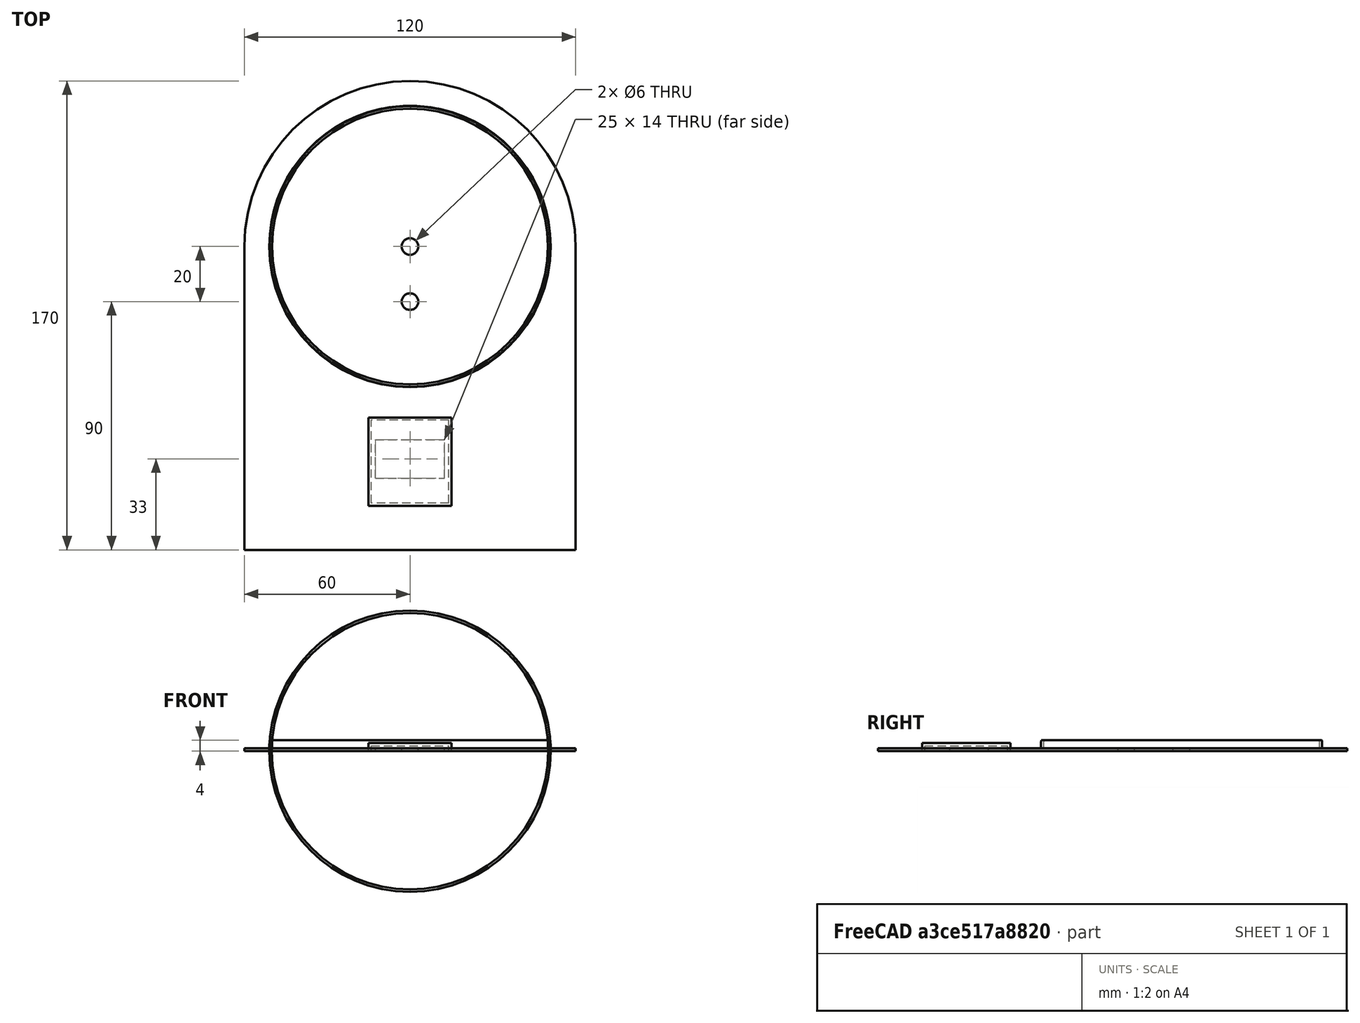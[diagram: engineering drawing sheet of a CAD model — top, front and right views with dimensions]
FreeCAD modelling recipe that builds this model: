
FCSTD DOCUMENT  (FreeCAD 0.16R6703 (Git))
Label: moon_support_v2
License: CreativeCommons Attribution-ShareAlike
LicenseURL: http://creativecommons.org/licenses/by-sa/4.0/
objects: Part::Box×5, Part::Cut×5, Part::Cylinder×3, Part::Sphere×2, Part::MultiFuse×2
note: 17 computed .brp shape members not serialized (recipe doc carries the construction recipe); baked Part::Feature solids carry a one-line shape summary decoded from their .brp

FEATURE [Part::Sphere] Sphere  label="moon"
  Angle1 = -90
  Angle2 = 90
  Angle3 = 180
  Placement = pos=(0,0,0) rot=(1,0,0;1.5708rad)
  Radius = 50.1
FEATURE [Part::Sphere] Sphere001  label="moon_cover"
  Angle1 = -90
  Angle2 = 90
  Angle3 = 180
  Placement = pos=(0,0,0) rot=(1,0,0;1.5708rad)
  Radius = 51
FEATURE [Part::Box] Box  label="recote_soporte"
  Height = 120
  Length = 120
  Placement = pos=(-60,-60,4) rot=(0,0,1;0rad)
  Width = 120
FEATURE [Part::Cut] Cut
  Base = -> Sphere001
  Tool = -> Sphere
FEATURE [Part::Cut] Cut001
  Base = -> Cut
  Tool = -> Box
FEATURE [Part::Cylinder] Cylinder
  Angle = 360
  Height = 20
  Placement = pos=(0,-20,-2) rot=(0,0,1;0rad)
  Radius = 3
FEATURE [Part::Box] Box001  label="Cube"
  Height = 1
  Length = 120
  Placement = pos=(-60,-110,0) rot=(0,0,1;0rad)
  Width = 110
FEATURE [Part::Cylinder] Cylinder001
  Angle = 360
  Height = 1
  Radius = 60
FEATURE [Part::Box] Box002  label="lcd"
  Height = 10
  Length = 25
  Placement = pos=(-12.5,-84,0) rot=(0,0,1;0rad)
  Width = 14
FEATURE [Part::Box] Box003  label="pcb_lcd"
  Height = 3
  Length = 28
  Placement = pos=(-14,-93,-1) rot=(0,0,1;0rad)
  Width = 30
FEATURE [Part::Box] Box004  label="pcb_lcd001"
  Height = 3
  Length = 30
  Placement = pos=(-15,-94,0) rot=(0,0,1;0rad)
  Width = 32
FEATURE [Part::Cut] Cut002
  Base = -> Box004
  Tool = -> Box003
FEATURE [Part::MultiFuse] Fusion
  Shapes = -> [Cut001,Cylinder001,Box001]
FEATURE [Part::MultiFuse] Fusion001
  Shapes = -> [Box002,Cylinder]
FEATURE [Part::Cut] Cut003
  Base = -> Fusion
  Tool = -> Fusion001
FEATURE [Part::Cylinder] Cylinder002
  Angle = 360
  Height = 20
  Placement = pos=(0,0,-2) rot=(0,0,1;0rad)
  Radius = 3
FEATURE [Part::Cut] Cut004
  Base = -> Cut003
  Tool = -> Cylinder002
